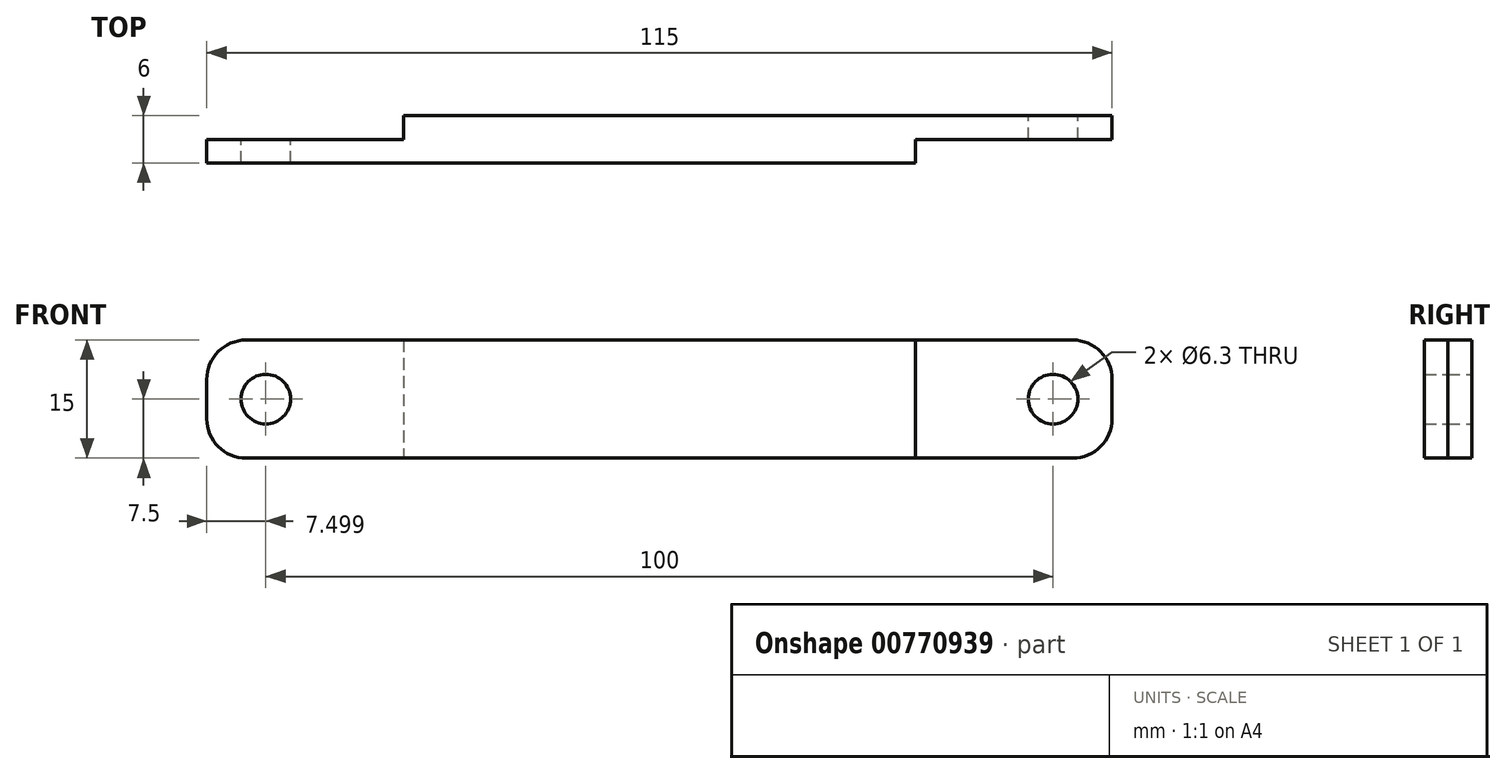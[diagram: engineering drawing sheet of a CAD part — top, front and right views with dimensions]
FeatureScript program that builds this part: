
annotation { "Feature Type Name" : "Feature", "Feature Type Description" : "" }
export const myFeature = defineFeature(function(context is Context, id is Id, definition is map)
    precondition{}
    {
        {
            var Q0;
            Q0=qCreatedBy(makeId("Front.planeOp"),FACE);
            var sketch = newSketch(context, id + "F0", { "sketchPlane" : qUnion([Q0])});
            skLineSegment(sketch, "E0.bottom", {"start": v(-58.54, 0) * mm, "end": v(56.46, 0) * mm});
            skLineSegment(sketch, "E0.top", {"start": v(-58.54, -15) * mm, "end": v(56.46, -15) * mm});
            skLineSegment(sketch, "E0.left", {"start": v(-58.54, 0) * mm, "end": v(-58.54, -15) * mm});
            skLineSegment(sketch, "E0.right", {"start": v(56.46, 0) * mm, "end": v(56.46, -15) * mm});
            skCircle(sketch, "E1", {"center": v(-51.04, -7.5) * mm, "radius": 3.15 * mm});
            skCircle(sketch, "E2", {"center": v(48.96, -7.5) * mm, "radius": 3.15 * mm});
            skSolve(sketch);
        }
        {
            var Q0;
            Q0 = qSketchRegion(id + "F0", true);
            extrude(context, id + "F1", {"entities" : qUnion([Q0]), "endBound" : BoundingType.SYMMETRIC, "depth" : 6 * mm, "offsetDistance" : 25 * mm});
        }
        {
            var Q0;
            Q0=qCreatedBy(makeId("Front.planeOp"),FACE);
            var sketch = newSketch(context, id + "F2", { "sketchPlane" : qUnion([Q0])});
            skLineSegment(sketch, "E3.bottom", {"start": v(-58.54, 0) * mm, "end": v(-33.54, 0) * mm});
            skLineSegment(sketch, "E3.top", {"start": v(-58.54, -15) * mm, "end": v(-33.54, -15) * mm});
            skLineSegment(sketch, "E3.left", {"start": v(-58.54, 0) * mm, "end": v(-58.54, -15) * mm});
            skLineSegment(sketch, "E3.right", {"start": v(-33.54, 0) * mm, "end": v(-33.54, -15) * mm});
            skSolve(sketch);
        }
        {
            var Q0;
            Q0=qCreatedBy(makeId("Front.planeOp"),FACE);
            var sketch = newSketch(context, id + "F3", { "sketchPlane" : qUnion([Q0])});
            skLineSegment(sketch, "E4.bottom", {"start": v(56.46, 0) * mm, "end": v(31.46, 0) * mm});
            skLineSegment(sketch, "E4.top", {"start": v(56.46, -15) * mm, "end": v(31.46, -15) * mm});
            skLineSegment(sketch, "E4.left", {"start": v(56.46, 0) * mm, "end": v(56.46, -15) * mm});
            skLineSegment(sketch, "E4.right", {"start": v(31.46, 0) * mm, "end": v(31.46, -15) * mm});
            skSolve(sketch);
        }
        {
            var Q0;
            Q0 = qSketchRegion(id + "F2", true);
            extrude(context, id + "F4", {"entities" : qUnion([Q0]), "operationType" : NewBodyOperationType.REMOVE, "oppositeDirection" : true, "depth" : 3 * mm, "offsetDistance" : 25 * mm});
        }
        {
            var Q0;
            Q0 = qSketchRegion(id + "F3", true);
            extrude(context, id + "F5", {"entities" : qUnion([Q0]), "operationType" : NewBodyOperationType.REMOVE, "depth" : 3 * mm, "offsetDistance" : 25 * mm});
        }
        {
            var Q0;
            Q0=makeQuery(id+"F1.opExtrude","SWEPT_EDGE",EDGE,{"disambiguationData":[OSD([sQuery(id+"F0.wireOp",EDGE,"E0.bottom"),sQuery(id+"F0.wireOp",EDGE,"E0.left")])]});
            var Q1;
            Q1=makeQuery(id+"F1.opExtrude","SWEPT_EDGE",EDGE,{"disambiguationData":[OSD([sQuery(id+"F0.wireOp",EDGE,"E0.top"),sQuery(id+"F0.wireOp",EDGE,"E0.left")])]});
            var Q2;
            Q2=makeQuery(id+"F1.opExtrude","SWEPT_EDGE",EDGE,{"disambiguationData":[OSD([sQuery(id+"F0.wireOp",EDGE,"E0.top"),sQuery(id+"F0.wireOp",EDGE,"E0.right")])]});
            var Q3;
            Q3=makeQuery(id+"F1.opExtrude","SWEPT_EDGE",EDGE,{"disambiguationData":[OSD([sQuery(id+"F0.wireOp",EDGE,"E0.bottom"),sQuery(id+"F0.wireOp",EDGE,"E0.right")])]});
            fillet(context, id + "F6", {"entities" : qUnion([Q0, Q1, Q2, Q3]), "radius" : 5 * mm, "tangentPropagation" : true, "allowEdgeOverflow" : false});
        }
    });
